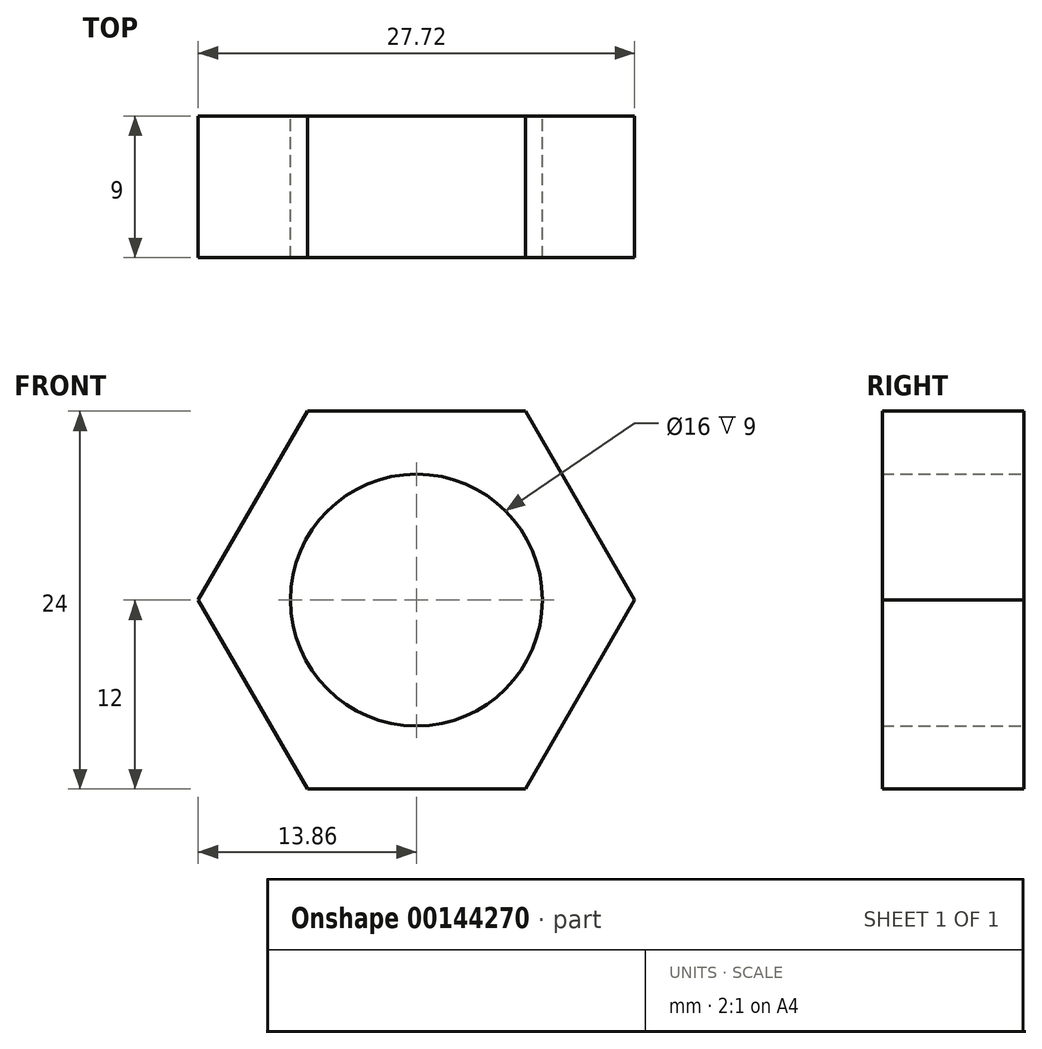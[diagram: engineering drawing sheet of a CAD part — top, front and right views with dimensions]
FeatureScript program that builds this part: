
annotation { "Feature Type Name" : "Feature", "Feature Type Description" : "" }
export const myFeature = defineFeature(function(context is Context, id is Id, definition is map)
    precondition{}
    {
        {
            var Q0;
            Q0=qCreatedBy(makeId("Front.planeOp"),FACE);
            var sketch = newSketch(context, id + "F0", { "sketchPlane" : qUnion([Q0])});
            skLineSegment(sketch, "E0", {"start": v(-17.83, 0) * mm, "end": v(24.73, 0) * mm, "construction": true});
            skLineSegment(sketch, "E1", {"start": v(-13.86, 0) * mm, "end": v(-6.93, 12) * mm});
            skLineSegment(sketch, "E2", {"start": v(-6.93, 12) * mm, "end": v(6.93, 12) * mm});
            skLineSegment(sketch, "E3", {"start": v(6.93, 12) * mm, "end": v(13.86, 0) * mm});
            skLineSegment(sketch, "E4", {"start": v(-13.86, 0) * mm, "end": v(-6.93, -12) * mm});
            skLineSegment(sketch, "E5", {"start": v(-6.93, -12) * mm, "end": v(6.93, -12) * mm});
            skLineSegment(sketch, "E6", {"start": v(6.93, -12) * mm, "end": v(13.86, 0) * mm});
            skLineSegment(sketch, "E7", {"start": v(0, 38.05) * mm, "end": v(0, -28.27) * mm, "construction": true});
            skPoint(sketch, "E7.endSnap0", {"position": v(0, 12) * mm});
            skCircle(sketch, "E8", {"center": v(0, 0) * mm, "radius": 8 * mm});
            skSolve(sketch);
        }
        {
            var Q0;
            Q0 = qSketchRegion(id + "F0", true);
            extrude(context, id + "F1", {"entities" : qUnion([Q0]), "depth" : 9 * mm});
        }
    });
